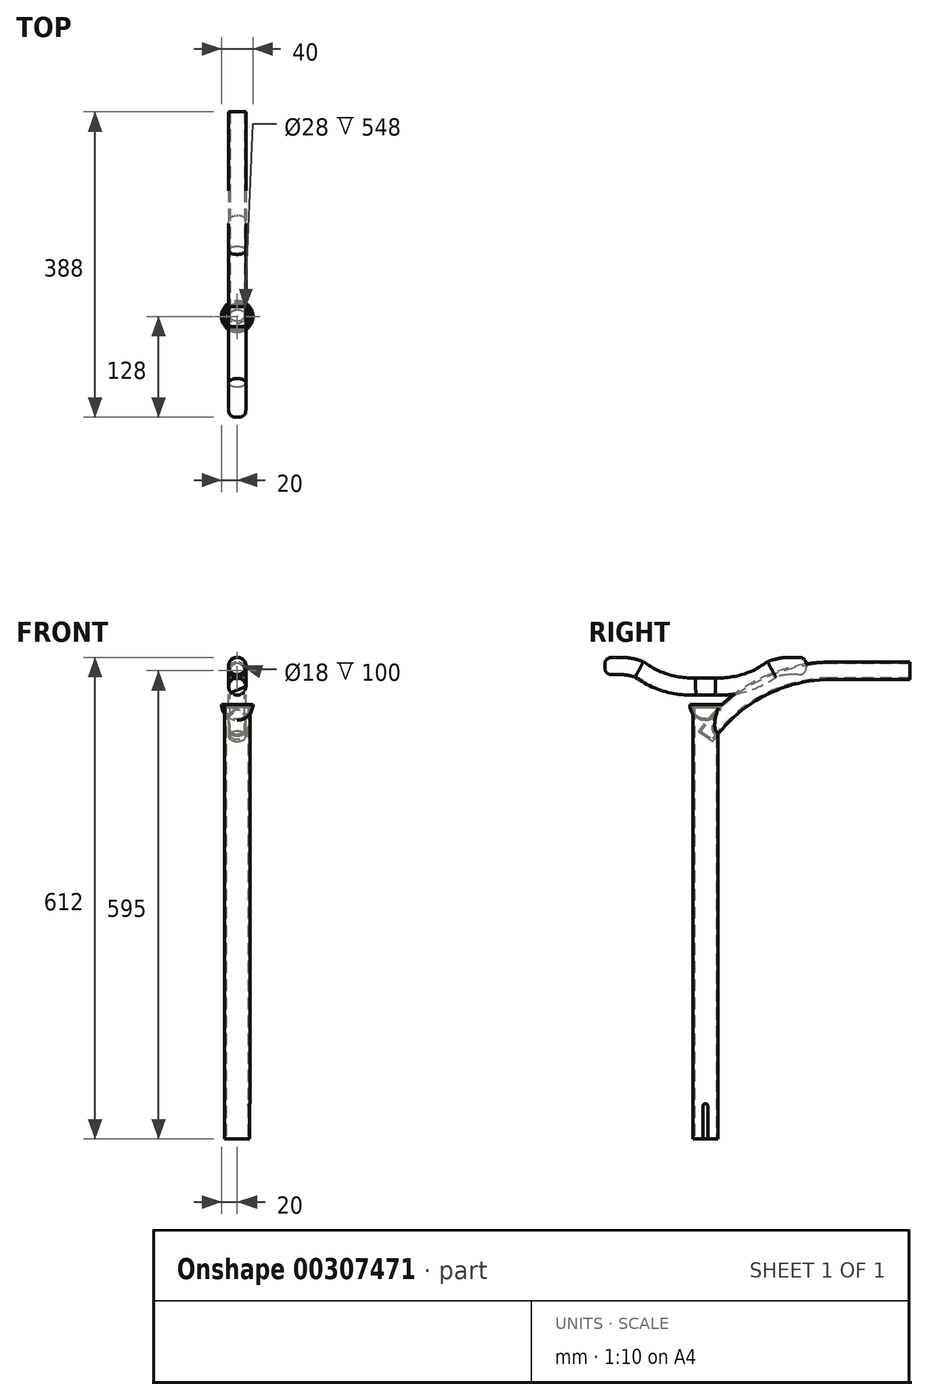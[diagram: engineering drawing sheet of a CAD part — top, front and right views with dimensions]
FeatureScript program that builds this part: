
annotation { "Feature Type Name" : "Feature", "Feature Type Description" : "" }
export const myFeature = defineFeature(function(context is Context, id is Id, definition is map)
    precondition{}
    {
        {
            var Q0;
            Q0=qCreatedBy(makeId("Top.planeOp"),FACE);
            var sketch = newSketch(context, id + "F0", { "sketchPlane" : qUnion([Q0])});
            skCircle(sketch, "E0", {"center": v(0, 0) * mm, "radius": 16 * mm});
            skSolve(sketch);
        }
        {
            var Q0;
            Q0 = qSketchRegion(id + "F0", true);
            extrude(context, id + "F1", {"entities" : qUnion([Q0]), "depth" : 550 * mm, "offsetDistance" : 25 * mm});
        }
        {
            var Q0;
            Q0=makeQuery(id+"F1.opExtrude","CAP_FACE",FACE,{"disambiguationData":[OSD([sQuery(id+"F0.wireOp",EDGE,"E0")])],"isStart":true});
            shell(context, id + "F2", {"entities" : qUnion([Q0]), "thickness" : 2 * mm});
        }
        {
            var Q0;
            Q0=qCreatedBy(makeId("Right.planeOp"),FACE);
            var sketch = newSketch(context, id + "F3", { "sketchPlane" : qUnion([Q0])});
            skLineSegment(sketch, "E1", {"start": v(-3.15, 0) * mm, "end": v(2.85, 0) * mm});
            skLineSegment(sketch, "E2", {"start": v(2.85, 0) * mm, "end": v(2.85, 42) * mm});
            skLineSegment(sketch, "E3", {"start": v(-0.15, 45) * mm, "end": v(-0.15, 45) * mm});
            skLineSegment(sketch, "E4", {"start": v(-3.15, 42) * mm, "end": v(-3.15, 0) * mm});
            skArc(sketch, "E5.filletArc", {"start": v(-0.15, 45) * mm, "mid": v(-2.27, 44.12) * mm, "end": v(-3.15, 42) * mm});
            skArc(sketch, "E6.filletArc", {"start": v(2.85, 42) * mm, "mid": v(1.97, 44.12) * mm, "end": v(-0.15, 45) * mm});
            skSolve(sketch);
        }
        {
            var Q0;
            Q0 = qSketchRegion(id + "F3", true);
            extrude(context, id + "F4", {"entities" : qUnion([Q0]), "operationType" : NewBodyOperationType.REMOVE, "endBound" : BoundingType.THROUGH_ALL, "depth" : 25 * mm, "offsetDistance" : 25 * mm});
        }
        {
            var Q0;
            Q0=qCreatedBy(makeId("Right.planeOp"),FACE);
            var sketch = newSketch(context, id + "F5", { "sketchPlane" : qUnion([Q0])});
            skArc(sketch, "E7", {"start": v(160, 595) * mm, "mid": v(69.75, 572.86) * mm, "end": v(0, 511.47) * mm});
            skLineSegment(sketch, "E8", {"start": v(160, 595) * mm, "end": v(260, 595) * mm});
            skSolve(sketch);
        }
        {
            var Q0;
            Q0=sQuery(id+"F5.wireOp",VERTEX,"E8.end");
            var Q1;
            Q1=qCreatedBy(makeId("Front.planeOp"),FACE);
            cPlane(context, id + "F6", {"entities" : qUnion([Q0, Q1]), "cplaneType" : CPlaneType.PLANE_POINT, "offset" : 25 * mm, "width" : 150 * mm, "height" : 150 * mm});
        }
        {
            var Q0;
            Q0=qCreatedBy(id+"F6.planeOp",FACE);
            var sketch = newSketch(context, id + "F7", { "sketchPlane" : qUnion([Q0])});
            skCircle(sketch, "E9", {"center": v(0, 595) * mm, "radius": 11 * mm});
            skSolve(sketch);
        }
        {
            var Q0;
            Q0 = qSketchRegion(id + "F7", true);
            var Q1;
            Q1 = qConstructionFilter(qBodyType(qCreatedBy(id + "F5" ,EDGE), BodyType.WIRE), ConstructionObject.NO);
            sweep(context, id + "F8", {"operationType" : NewBodyOperationType.ADD, "profiles" : qUnion([Q0]), "path" : qUnion([Q1])});
        }
        {
            var Q0;
            Q0=makeQuery(id+"F8.opSweep","CAP_FACE",FACE,{"disambiguationData":[OSD([sQuery(id+"F5.wireOp",VERTEX,"E8.end"),sQuery(id+"F7.wireOp",EDGE,"E9")])],"isStart":true});
            shell(context, id + "F9", {"entities" : qUnion([Q0]), "thickness" : 2 * mm});
        }
        {
            var Q0;
            Q0=qCreatedBy(makeId("Right.planeOp"),FACE);
            var sketch = newSketch(context, id + "F10", { "sketchPlane" : qUnion([Q0])});
            skLineSegment(sketch, "E10", {"start": v(-128, 601) * mm, "end": v(-108, 601) * mm});
            skArc(sketch, "E11", {"start": v(-84.1, 596.7) * mm, "mid": v(-95.86, 599.92) * mm, "end": v(-108, 601) * mm});
            skArc(sketch, "E12", {"start": v(-84.1, 596.7) * mm, "mid": v(-50.16, 579.7) * mm, "end": v(-12.5, 575) * mm});
            skLineSegment(sketch, "E13", {"start": v(-12.5, 575) * mm, "end": v(0, 575) * mm});
            skLineSegment(sketch, "E14.MirrorCS", {"start": v(12.5, 575) * mm, "end": v(0, 575) * mm});
            skArc(sketch, "E15.MirrorCS", {"start": v(84.1, 596.7) * mm, "mid": v(50.16, 579.7) * mm, "end": v(12.5, 575) * mm});
            skArc(sketch, "E16.MirrorCS", {"start": v(84.1, 596.7) * mm, "mid": v(95.86, 599.92) * mm, "end": v(108, 601) * mm});
            skLineSegment(sketch, "E17.MirrorCS", {"start": v(128, 601) * mm, "end": v(108, 601) * mm});
            skSolve(sketch);
        }
        {
            var Q0;
            Q0=sQuery(id+"F10.wireOp",VERTEX,"E17.MirrorCS.start");
            var Q1;
            Q1=qCreatedBy(id+"F6.planeOp",FACE);
            cPlane(context, id + "F11", {"entities" : qUnion([Q0, Q1]), "cplaneType" : CPlaneType.PLANE_POINT, "offset" : 25 * mm, "width" : 150 * mm, "height" : 150 * mm});
        }
        {
            var Q0;
            Q0=qCreatedBy(id+"F11.planeOp",FACE);
            var sketch = newSketch(context, id + "F12", { "sketchPlane" : qUnion([Q0])});
            skCircle(sketch, "E18", {"center": v(0, 601) * mm, "radius": 11 * mm});
            skSolve(sketch);
        }
        {
            var Q0;
            Q0 = qSketchRegion(id + "F12", true);
            var Q1;
            Q1 = qConstructionFilter(qBodyType(qCreatedBy(id + "F10" ,EDGE), BodyType.WIRE), ConstructionObject.NO);
            sweep(context, id + "F13", {"profiles" : qUnion([Q0]), "path" : qUnion([Q1])});
        }
        {
            var Q0;
            Q0=makeQuery(id+"F13.opSweep","CAP_EDGE",EDGE,{"disambiguationData":[OSD([sQuery(id+"F10.wireOp",VERTEX,"E10.start"),sQuery(id+"F12.wireOp",EDGE,"E18")])],"isStart":false});
            var Q1;
            Q1=makeQuery(id+"F13.opSweep","CAP_EDGE",EDGE,{"disambiguationData":[OSD([sQuery(id+"F10.wireOp",VERTEX,"E17.MirrorCS.start"),sQuery(id+"F12.wireOp",EDGE,"E18")])],"isStart":true});
            fillet(context, id + "F14", {"entities" : qUnion([Q0, Q1]), "radius" : 10 * mm, "tangentPropagation" : true, "rho" : 0.5, "crossSection" : FilletCrossSection.CONIC, "allowEdgeOverflow" : false});
        }
        {
            var Q0;
            Q0=qCreatedBy(makeId("Right.planeOp"),FACE);
            var sketch = newSketch(context, id + "F15", { "sketchPlane" : qUnion([Q0])});
            skArc(sketch, "E19", {"start": v(-20, 552) * mm, "mid": v(-14.14, 537.86) * mm, "end": v(0, 532) * mm});
            skLineSegment(sketch, "E20", {"start": v(0, 552) * mm, "end": v(0, 532) * mm});
            skLineSegment(sketch, "E21", {"start": v(0, 552) * mm, "end": v(-20, 552) * mm});
            skPoint(sketch, "E22.orphan", {"position": v(0, 572) * mm});
            skSolve(sketch);
        }
        {
            var Q0;
            Q0 = qSketchRegion(id + "F15", true);
            var Q1;
            Q1=sQuery(id+"F15.wireOp",EDGE,"E20");
            revolve(context, id + "F16", {"entities" : qUnion([Q0]), "axis" : qUnion([Q1]), "revolveType" : RevolveType.FULL});
        }
        {
            var Q0;
            Q0=makeQuery(id+"F16.opRevolve","SWEPT_FACE",FACE,{"disambiguationData":[OSD([sQuery(id+"F15.wireOp",EDGE,"E21")])]});
            shell(context, id + "F17", {"entities" : qUnion([Q0]), "thickness" : 2 * mm});
        }
    });
